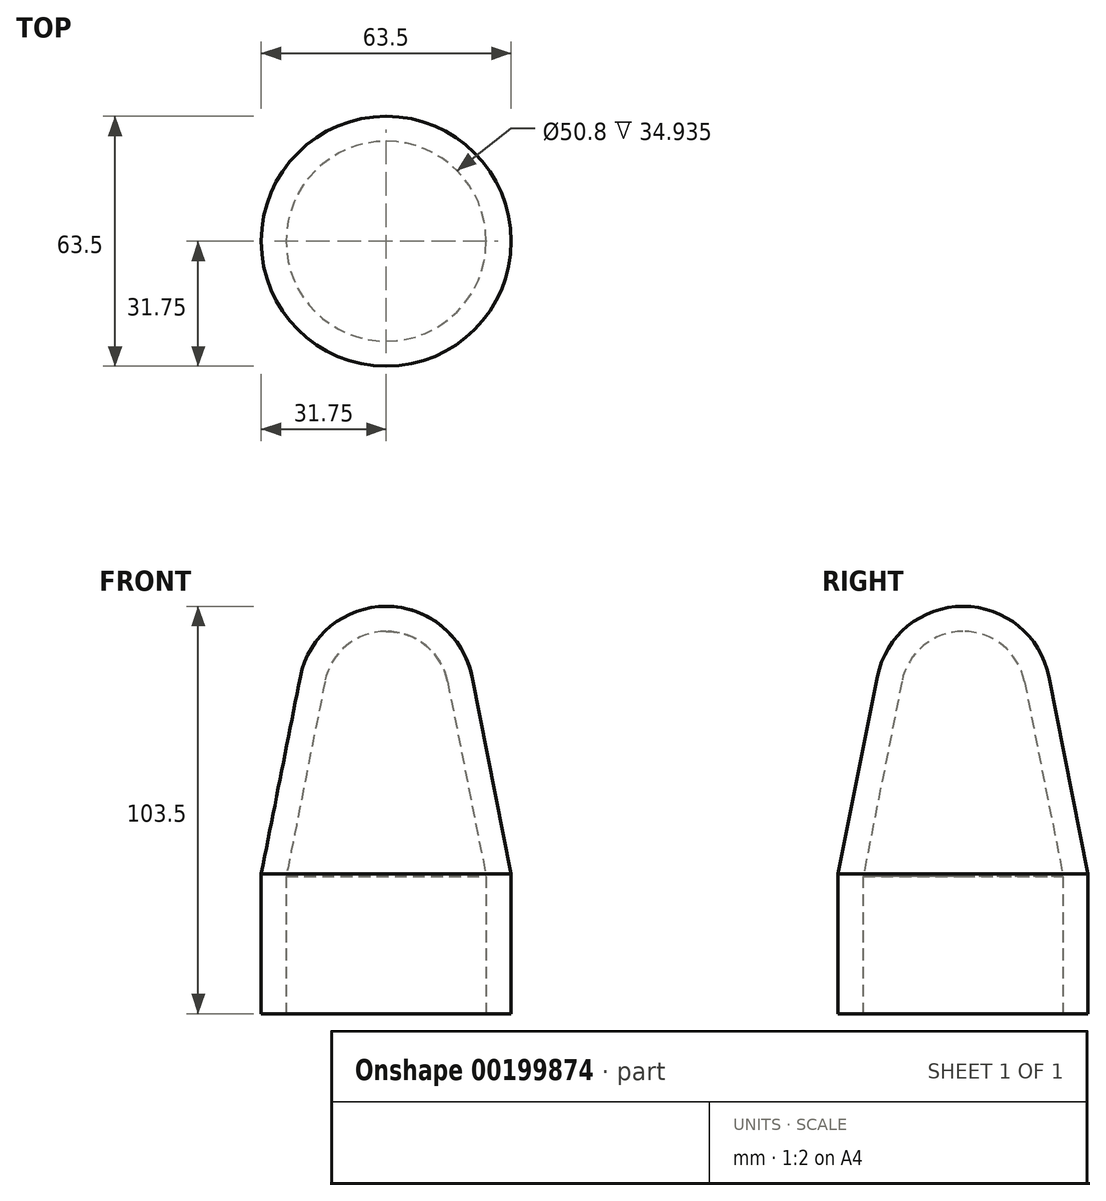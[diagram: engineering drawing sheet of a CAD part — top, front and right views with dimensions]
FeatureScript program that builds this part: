
annotation { "Feature Type Name" : "Feature", "Feature Type Description" : "" }
export const myFeature = defineFeature(function(context is Context, id is Id, definition is map)
    precondition{}
    {
        {
            var Q0;
            Q0=qCreatedBy(makeId("Front.planeOp"),FACE);
            var sketch = newSketch(context, id + "F0", { "sketchPlane" : qUnion([Q0])});
            skLineSegment(sketch, "E0.top", {"start": v(31.75, -17.78) * mm, "end": v(0, -17.78) * mm});
            skLineSegment(sketch, "E0.left", {"start": v(31.75, 17.78) * mm, "end": v(31.75, -17.78) * mm});
            skPoint(sketch, "E0.middle", {"position": v(0, 0) * mm});
            skArc(sketch, "E1", {"start": v(21.8, 67.83) * mm, "mid": v(14.1, 80.68) * mm, "end": v(0, 85.72) * mm});
            skLineSegment(sketch, "E2", {"start": v(31.75, 17.78) * mm, "end": v(21.8, 67.83) * mm});
            skLineSegment(sketch, "E3", {"start": v(0, -17.78) * mm, "end": v(0, -11.43) * mm});
            skPoint(sketch, "E3.endSnap0", {"position": v(0, 85.72) * mm});
            skPoint(sketch, "E0.right.start.orphan", {"position": v(-31.75, 17.78) * mm});
            skPoint(sketch, "E4.orphan", {"position": v(-31.75, -17.78) * mm});
            skArc(sketch, "E5.0", {"start": v(15.57, 66.6) * mm, "mid": v(10.07, 75.77) * mm, "end": v(0, 79.38) * mm});
            skLineSegment(sketch, "E5.1", {"start": v(25.4, 17.15) * mm, "end": v(15.57, 66.6) * mm});
            skLineSegment(sketch, "E5.2", {"start": v(25.4, 17.15) * mm, "end": v(25.4, -11.43) * mm});
            skLineSegment(sketch, "E5.3", {"start": v(25.4, -11.43) * mm, "end": v(0, -11.43) * mm});
            skLineSegment(sketch, "E6.trimOffspring", {"start": v(0, 79.38) * mm, "end": v(0, 85.72) * mm});
            skSolve(sketch);
        }
        {
            var Q0;
            Q0=makeQuery(id+"F0.imprint","IMPRINT",FACE,{"disambiguationData":[TD([[makeQuery(id+"F0.imprint","IMPRINT",EDGE,{"derivedFrom":sQuery(id+"F0.wireOp",EDGE,"E0.top")}),-1.0]])]});
            var Q1;
            Q1=sQuery(id+"F0.wireOp",EDGE,"E3");
            revolve(context, id + "F1", {"entities" : qUnion([Q0]), "axis" : qUnion([Q1]), "revolveType" : RevolveType.FULL});
        }
        {
            var Q0;
            Q0=makeQuery(id+"F1.opRevolve","SWEPT_FACE",FACE,{"disambiguationData":[OSD([sQuery(id+"F0.wireOp",EDGE,"E0.top")])]});
            var sketch = newSketch(context, id + "F2", { "sketchPlane" : qUnion([Q0])});
            skCircle(sketch, "E7.0", {"center": v(0, 0) * mm, "radius": 25.4 * mm});
            skSolve(sketch);
        }
        {
            var Q0;
            Q0 = qSketchRegion(id + "F2", true);
            extrude(context, id + "F3", {"entities" : qUnion([Q0]), "operationType" : NewBodyOperationType.REMOVE, "oppositeDirection" : true, "depth" : 12.7 * mm});
        }
    });
